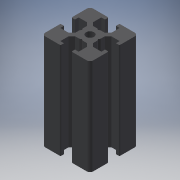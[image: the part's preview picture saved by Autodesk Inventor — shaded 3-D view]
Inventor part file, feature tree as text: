
AUTODESK INVENTOR PART (.ipt)
format: ipt  version: 2016 (Build 200138000, 138)  size: 168,960 bytes
history: native  units: mm
features: extrude x1, sketch x1
ambient origin geometry x8: Origin, YZ Plane, XZ Plane, XY Plane, X Axis, Y Axis, Z Axis, Center Point
bodies: Solid1 (feature_tree)
feature tree (2):
  extrude  "Extrusion1"  [1 undecoded]
  sketch  "Sketch_1"  dims[d0=30.0mm d1=0.0mm]
note: 1 required parameter value undecoded (feature->parameter linkage not recoverable at this tier; creation-order binding heuristic only, values carry confidence <= 0.55)
